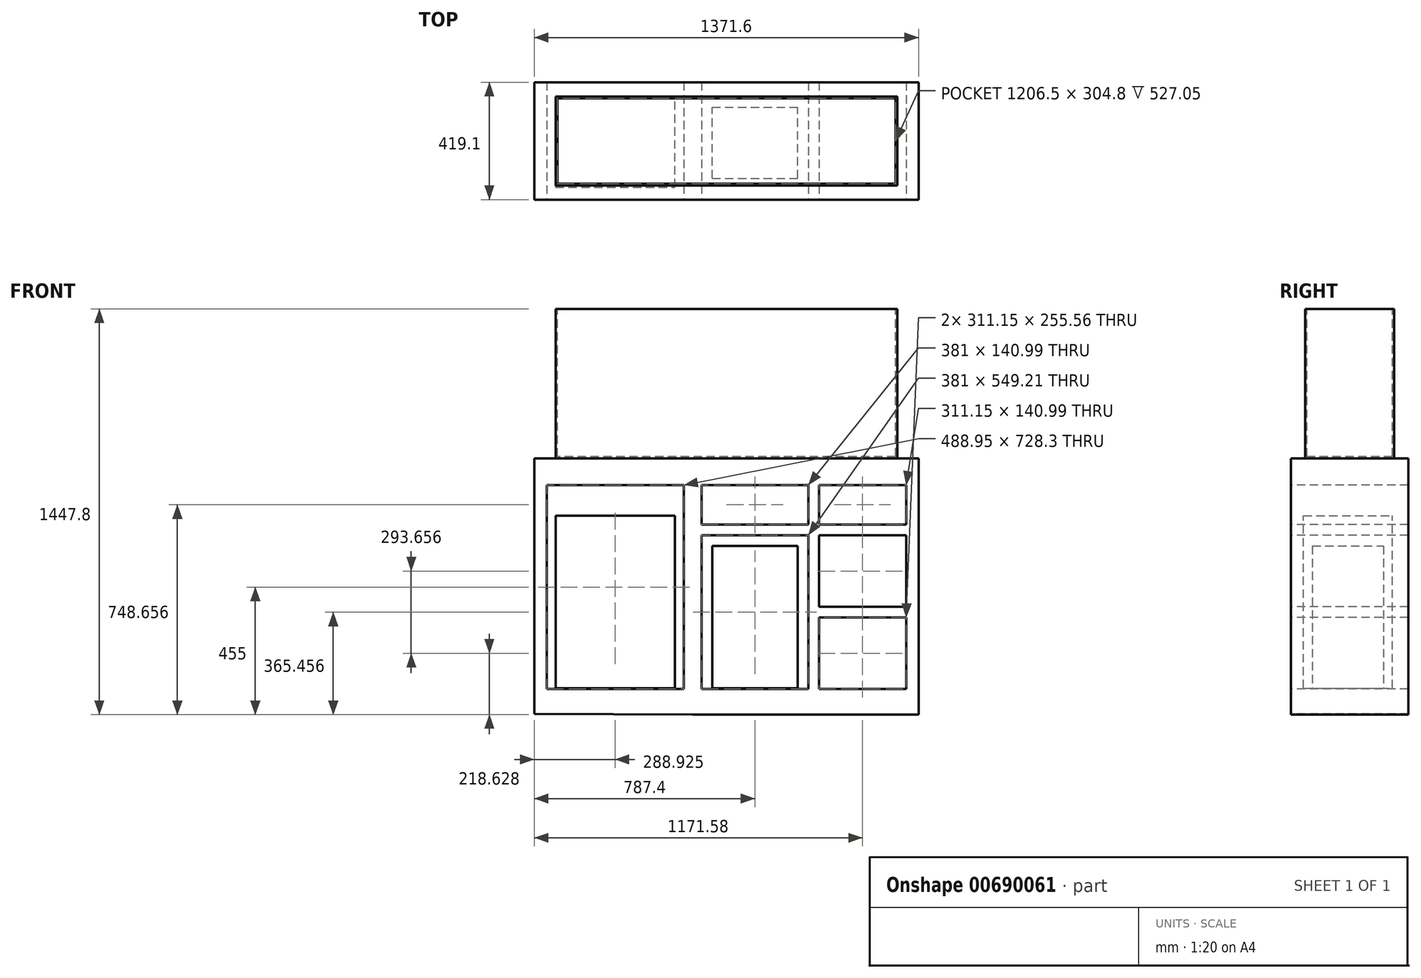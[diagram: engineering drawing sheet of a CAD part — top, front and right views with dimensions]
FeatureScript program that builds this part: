
annotation { "Feature Type Name" : "Feature", "Feature Type Description" : "" }
export const myFeature = defineFeature(function(context is Context, id is Id, definition is map)
    precondition{}
    {
        {
            var Q0;
            Q0=qCreatedBy(makeId("Front.planeOp"),FACE);
            var sketch = newSketch(context, id + "F0", { "sketchPlane" : qUnion([Q0])});
            skLineSegment(sketch, "E0", {"start": v(0, 0) * mm, "end": v(0, 533.4) * mm});
            skLineSegment(sketch, "E1", {"start": v(0, 533.4) * mm, "end": v(1219.2, 533.4) * mm});
            skLineSegment(sketch, "E2", {"start": v(1219.2, 533.4) * mm, "end": v(1219.2, 0) * mm});
            skLineSegment(sketch, "E3", {"start": v(1219.2, 0) * mm, "end": v(0, 0) * mm});
            skSolve(sketch);
        }
        {
            var Q0;
            Q0 = qSketchRegion(id + "F0", true);
            extrude(context, id + "F1", {"entities" : qUnion([Q0]), "depth" : 317.5 * mm, "offsetDistance" : 25.4 * mm});
        }
        {
            var Q0;
            Q0=makeQuery(id+"F1.opExtrude","SWEPT_FACE",FACE,{"disambiguationData":[OSD([sQuery(id+"F0.wireOp",EDGE,"E1")])]});
            var sketch = newSketch(context, id + "F2", { "sketchPlane" : qUnion([Q0])});
            skLineSegment(sketch, "E4", {"start": v(6.35, -6.35) * mm, "end": v(6.35, -311.15) * mm});
            skLineSegment(sketch, "E5", {"start": v(6.35, -311.15) * mm, "end": v(1212.85, -311.15) * mm});
            skLineSegment(sketch, "E6", {"start": v(1212.85, -311.15) * mm, "end": v(1212.85, -6.35) * mm});
            skLineSegment(sketch, "E7", {"start": v(1212.85, -6.35) * mm, "end": v(6.35, -6.35) * mm});
            skSolve(sketch);
        }
        {
            var Q0;
            Q0 = qSketchRegion(id + "F2", true);
            extrude(context, id + "F3", {"entities" : qUnion([Q0]), "operationType" : NewBodyOperationType.REMOVE, "oppositeDirection" : true, "depth" : 527.05 * mm, "offsetDistance" : 25.4 * mm});
        }
        {
            var Q0;
            Q0=makeQuery(id+"F1.opExtrude","CAP_FACE",FACE,{"disambiguationData":[OSD([sQuery(id+"F0.wireOp",EDGE,"E0"),sQuery(id+"F0.wireOp",EDGE,"E1"),sQuery(id+"F0.wireOp",EDGE,"E2"),sQuery(id+"F0.wireOp",EDGE,"E3")])],"isStart":false});
            var sketch = newSketch(context, id + "F4", { "sketchPlane" : qUnion([Q0])});
            skLineSegment(sketch, "E8", {"start": v(-76.2, 0) * mm, "end": v(1295.4, 0) * mm});
            skLineSegment(sketch, "E9", {"start": v(488.95, 0) * mm, "end": v(488.95, -914.4) * mm});
            skLineSegment(sketch, "E10", {"start": v(-76.2, 0) * mm, "end": v(-76.2, -912.45) * mm});
            skLineSegment(sketch, "E11", {"start": v(-76.2, -912.45) * mm, "end": v(488.95, -914.4) * mm});
            skLineSegment(sketch, "E12", {"start": v(1295.4, -914.4) * mm, "end": v(488.95, -914.4) * mm});
            skLineSegment(sketch, "E13", {"start": v(1295.4, 0) * mm, "end": v(1295.4, -914.4) * mm});
            skLineSegment(sketch, "E14", {"start": v(-76.2, -95.25) * mm, "end": v(1295.4, -95.25) * mm});
            skLineSegment(sketch, "E15", {"start": v(-76.2, -823.55) * mm, "end": v(1295.4, -823.55) * mm});
            skLineSegment(sketch, "E16", {"start": v(457.2, 0) * mm, "end": v(457.2, -914.4) * mm});
            skLineSegment(sketch, "E17", {"start": v(520.7, 0) * mm, "end": v(520.7, -912.45) * mm});
            skLineSegment(sketch, "E18", {"start": v(-31.75, 0) * mm, "end": v(-31.75, -912.45) * mm});
            skLineSegment(sketch, "E19", {"start": v(1250.95, 0) * mm, "end": v(1250.95, -914.4) * mm});
            skSolve(sketch);
        }
        {
            var Q0;
            {var subQ0=sQuery(id+"F4.wireOp",EDGE,"E14");var subQ1=sQuery(id+"F4.wireOp",EDGE,"E10");var subQ2=makeQuery(id+"F4.imprint","INTERSECT",VERTEX,{"derivedFrom":[subQ1,subQ0]});Q0=makeQuery(id+"F4.imprint","IMPRINT",FACE,{"disambiguationData":[TD([[makeQuery(id+"F4.imprint","IMPRINT",EDGE,{"disambiguationData":[TD([[subQ2,-1.0]])],"derivedFrom":subQ1}),1.0]])]});}
            var Q1;
            {var subQ1=sQuery(id+"F4.wireOp",EDGE,"E10");var subQ4=sQuery(id+"F4.wireOp",EDGE,"E11");var subQ5=makeQuery(id+"F4.imprint","INTERSECT",VERTEX,{"derivedFrom":[subQ1,subQ4]});Q1=makeQuery(id+"F4.imprint","IMPRINT",FACE,{"disambiguationData":[TD([[makeQuery(id+"F4.imprint","IMPRINT",EDGE,{"disambiguationData":[TD([[subQ5,1.0]])],"derivedFrom":subQ1}),1.0]])]});}
            var Q2;
            {var subQ0=sQuery(id+"F4.wireOp",EDGE,"E14");var subQ1=sQuery(id+"F4.wireOp",EDGE,"E9");var subQ2=makeQuery(id+"F4.imprint","INTERSECT",VERTEX,{"derivedFrom":[subQ1,subQ0]});Q2=makeQuery(id+"F4.imprint","IMPRINT",FACE,{"disambiguationData":[TD([[makeQuery(id+"F4.imprint","IMPRINT",EDGE,{"disambiguationData":[TD([[subQ2,-1.0]])],"derivedFrom":subQ1}),-1.0]])]});}
            var Q3;
            {var subQ0=sQuery(id+"F4.wireOp",EDGE,"E14");var subQ1=sQuery(id+"F4.wireOp",EDGE,"E9");var subQ2=makeQuery(id+"F4.imprint","INTERSECT",VERTEX,{"derivedFrom":[subQ1,subQ0]});Q3=makeQuery(id+"F4.imprint","IMPRINT",FACE,{"disambiguationData":[TD([[makeQuery(id+"F4.imprint","IMPRINT",EDGE,{"disambiguationData":[TD([[subQ2,-1.0]])],"derivedFrom":subQ1}),1.0]])]});}
            var Q4;
            {var subQ1=sQuery(id+"F4.wireOp",EDGE,"E9");var subQ3=sQuery(id+"F4.wireOp",EDGE,"E15");var subQ4=makeQuery(id+"F4.imprint","INTERSECT",VERTEX,{"derivedFrom":[subQ1,subQ3]});Q4=makeQuery(id+"F4.imprint","IMPRINT",FACE,{"disambiguationData":[TD([[makeQuery(id+"F4.imprint","IMPRINT",EDGE,{"disambiguationData":[TD([[subQ4,1.0]])],"derivedFrom":subQ3}),-1.0]])]});}
            var Q5;
            {var subQ0=sQuery(id+"F4.wireOp",EDGE,"E15");var subQ1=makeQuery(id+"F4.imprint","INTERSECT",VERTEX,{"derivedFrom":[subQ0,sQuery(id+"F4.wireOp",EDGE,"E17")]});Q5=makeQuery(id+"F4.imprint","IMPRINT",FACE,{"disambiguationData":[TD([[makeQuery(id+"F4.imprint","IMPRINT",EDGE,{"disambiguationData":[TD([[subQ1,1.0]])],"derivedFrom":subQ0}),-1.0]])]});}
            var Q6;
            {var subQ0=sQuery(id+"F4.wireOp",EDGE,"E13");var subQ1=sQuery(id+"F4.wireOp",EDGE,"E12");var subQ2=makeQuery(id+"F4.imprint","INTERSECT",VERTEX,{"derivedFrom":[subQ1,subQ0]});Q6=makeQuery(id+"F4.imprint","IMPRINT",FACE,{"disambiguationData":[TD([[makeQuery(id+"F4.imprint","IMPRINT",EDGE,{"disambiguationData":[TD([[subQ2,-1.0]])],"derivedFrom":subQ1}),-1.0]])]});}
            var Q7;
            {var subQ0=sQuery(id+"F4.wireOp",EDGE,"E14");var subQ1=sQuery(id+"F4.wireOp",EDGE,"E13");var subQ2=makeQuery(id+"F4.imprint","INTERSECT",VERTEX,{"derivedFrom":[subQ1,subQ0]});Q7=makeQuery(id+"F4.imprint","IMPRINT",FACE,{"disambiguationData":[TD([[makeQuery(id+"F4.imprint","IMPRINT",EDGE,{"disambiguationData":[TD([[subQ2,-1.0]])],"derivedFrom":subQ1}),-1.0]])]});}
            var Q8;
            {var subQ0=sQuery(id+"F4.wireOp",EDGE,"E13");var subQ1=sQuery(id+"F4.wireOp",EDGE,"E8");var subQ2=makeQuery(id+"F4.imprint","INTERSECT",VERTEX,{"derivedFrom":[subQ1,subQ0]});Q8=makeQuery(id+"F4.imprint","IMPRINT",FACE,{"disambiguationData":[TD([[makeQuery(id+"F4.imprint","IMPRINT",EDGE,{"disambiguationData":[TD([[subQ2,1.0]])],"derivedFrom":subQ1}),-1.0]])]});}
            var Q9;
            {var subQ0=sQuery(id+"F4.wireOp",EDGE,"E17");var subQ1=sQuery(id+"F4.wireOp",EDGE,"E8");var subQ2=makeQuery(id+"F4.imprint","INTERSECT",VERTEX,{"derivedFrom":[subQ1,subQ0]});Q9=makeQuery(id+"F4.imprint","IMPRINT",FACE,{"disambiguationData":[TD([[makeQuery(id+"F4.imprint","IMPRINT",EDGE,{"disambiguationData":[TD([[subQ2,1.0]])],"derivedFrom":subQ1}),1.0]])]});}
            var Q10;
            {var subQ1=sQuery(id+"F4.wireOp",EDGE,"E8");var subQ5=sQuery(id+"F4.wireOp",EDGE,"E18");var subQ8=makeQuery(id+"F4.imprint","INTERSECT",VERTEX,{"derivedFrom":[subQ1,subQ5]});Q10=makeQuery(id+"F4.imprint","IMPRINT",FACE,{"disambiguationData":[TD([[makeQuery(id+"F4.imprint","IMPRINT",EDGE,{"disambiguationData":[TD([[subQ8,-1.0]])],"derivedFrom":subQ1}),-1.0]])]});}
            var Q11;
            {var subQ0=sQuery(id+"F4.wireOp",EDGE,"E10");var subQ1=sQuery(id+"F4.wireOp",EDGE,"E8");var subQ2=makeQuery(id+"F4.imprint","INTERSECT",VERTEX,{"derivedFrom":[subQ1,subQ0]});Q11=makeQuery(id+"F4.imprint","IMPRINT",FACE,{"disambiguationData":[TD([[makeQuery(id+"F4.imprint","IMPRINT",EDGE,{"disambiguationData":[TD([[subQ2,-1.0]])],"derivedFrom":subQ1}),-1.0]])]});}
            var Q12;
            {var subQ0=sQuery(id+"F4.wireOp",EDGE,"E9");var subQ1=sQuery(id+"F4.wireOp",EDGE,"E8");var subQ2=makeQuery(id+"F4.imprint","INTERSECT",VERTEX,{"derivedFrom":[subQ1,subQ0]});Q12=makeQuery(id+"F4.imprint","IMPRINT",FACE,{"disambiguationData":[TD([[makeQuery(id+"F4.imprint","IMPRINT",EDGE,{"disambiguationData":[TD([[subQ2,1.0]])],"derivedFrom":subQ1}),1.0]])]});}
            var Q13;
            {var subQ0=sQuery(id+"F4.wireOp",EDGE,"E9");var subQ1=sQuery(id+"F4.wireOp",EDGE,"E8");var subQ2=makeQuery(id+"F4.imprint","INTERSECT",VERTEX,{"derivedFrom":[subQ1,subQ0]});Q13=makeQuery(id+"F4.imprint","IMPRINT",FACE,{"disambiguationData":[TD([[makeQuery(id+"F4.imprint","IMPRINT",EDGE,{"disambiguationData":[TD([[subQ2,-1.0]])],"derivedFrom":subQ1}),1.0]])]});}
            extrude(context, id + "F5", {"entities" : qUnion([Q0, Q1, Q2, Q3, Q4, Q5, Q6, Q7, Q8, Q9, Q10, Q11, Q12, Q13]), "operationType" : NewBodyOperationType.ADD, "oppositeDirection" : true, "depth" : 368.3 * mm, "offsetDistance" : 25.4 * mm, "hasSecondDirection" : true, "secondDirectionOppositeDirection" : false, "secondDirectionDepth" : 50.8 * mm});
        }
        {
            var Q0;
            Q0=makeQuery(id+"F5.opExtrude","CAP_FACE",FACE,{"disambiguationData":[OSD([sQuery(id+"F4.wireOp",EDGE,"E8"),sQuery(id+"F4.wireOp",EDGE,"E10"),sQuery(id+"F4.wireOp",EDGE,"E11"),sQuery(id+"F4.wireOp",EDGE,"E12"),sQuery(id+"F4.wireOp",EDGE,"E13"),sQuery(id+"F4.wireOp",EDGE,"E14"),sQuery(id+"F4.wireOp",EDGE,"E15"),sQuery(id+"F4.wireOp",EDGE,"E18"),sQuery(id+"F4.wireOp",EDGE,"E19")])],"isStart":true});
            var sketch = newSketch(context, id + "F6", { "sketchPlane" : qUnion([Q0])});
            skSolve(sketch);
        }
        {
            var Q0;
            {var subQ0=sQuery(id+"F4.wireOp",EDGE,"E15");Q0=makeQuery(id+"FelftkuU2XWx3Qa_1.boolean.opBoolean","MERGE",FACE,{"derivedFrom":[makeQuery(id+"F5.opExtrude","CAP_FACE",FACE,{"disambiguationData":[OSD([sQuery(id+"F4.wireOp",EDGE,"E8"),sQuery(id+"F4.wireOp",EDGE,"E10"),sQuery(id+"F4.wireOp",EDGE,"E11"),sQuery(id+"F4.wireOp",EDGE,"E12"),sQuery(id+"F4.wireOp",EDGE,"E13"),sQuery(id+"F4.wireOp",EDGE,"E14"),subQ0,sQuery(id+"F4.wireOp",EDGE,"E18"),sQuery(id+"F4.wireOp",EDGE,"E19")])],"isStart":true}),makeQuery(id+"FelftkuU2XWx3Qa_1.opExtrude","CAP_FACE",FACE,{"disambiguationData":[OSD([subQ0,sQuery(id+"F6.wireOp",EDGE,"Hjd6XBfF-dVlF-Pm7Q-uADI-go517BE28nij"),sQuery(id+"F6.wireOp",EDGE,"cSgCX02E-Zrxk-a7Yq-Ogc6-joIkRk6Krvnl"),sQuery(id+"F6.wireOp",EDGE,"0acloNvj-Bg05-ruuI-fCY6-iIz3YAx0FRrr"),sQuery(id+"F6.wireOp",EDGE,"pUvd6JdS-TNx4-0T37-JsWi-MApJu50DnG9t")])],"isStart":true})]});}
            cPlane(context, id + "F7", {"entities" : qUnion([Q0]), "cplaneType" : CPlaneType.OFFSET, "offset" : 203.2 * mm, "oppositeDirection" : true, "width" : 152.4 * mm, "height" : 152.4 * mm});
        }
        {
            var Q0;
            Q0=qCreatedBy(id+"F7.planeOp",FACE);
            var sketch = newSketch(context, id + "F8", { "sketchPlane" : qUnion([Q0])});
            skLineSegment(sketch, "E20.bottom", {"start": v(0, -820.44) * mm, "end": v(425.45, -820.44) * mm});
            skLineSegment(sketch, "E20.top", {"start": v(0, -204.49) * mm, "end": v(425.45, -204.49) * mm});
            skLineSegment(sketch, "E20.left", {"start": v(0, -820.44) * mm, "end": v(0, -204.49) * mm});
            skLineSegment(sketch, "E20.right", {"start": v(425.45, -820.44) * mm, "end": v(425.45, -204.49) * mm});
            skSolve(sketch);
        }
        {
            var Q0;
            Q0 = qSketchRegion(id + "F8", true);
            extrude(context, id + "F9", {"entities" : qUnion([Q0]), "depth" : 158.75 * mm, "offsetDistance" : 25.4 * mm, "hasSecondDirection" : true, "secondDirectionOppositeDirection" : true, "secondDirectionDepth" : 158.75 * mm});
        }
        {
            var Q0;
            Q0=qCreatedBy(id+"F7.planeOp",FACE);
            var sketch = newSketch(context, id + "F10", { "sketchPlane" : qUnion([Q0])});
            skLineSegment(sketch, "E21.bottom", {"start": v(558.8, -312.44) * mm, "end": v(863.6, -312.44) * mm});
            skLineSegment(sketch, "E21.top", {"start": v(558.8, -820.44) * mm, "end": v(863.6, -820.44) * mm});
            skLineSegment(sketch, "E21.left", {"start": v(558.8, -312.44) * mm, "end": v(558.8, -820.44) * mm});
            skLineSegment(sketch, "E21.right", {"start": v(863.6, -312.44) * mm, "end": v(863.6, -820.44) * mm});
            skSolve(sketch);
        }
        {
            var Q0;
            Q0 = qSketchRegion(id + "F10", true);
            extrude(context, id + "F11", {"entities" : qUnion([Q0]), "depth" : 127 * mm, "offsetDistance" : 25.4 * mm, "hasSecondDirection" : true, "secondDirectionOppositeDirection" : true, "secondDirectionDepth" : 127 * mm});
        }
        {
            var Q0;
            Q0=makeQuery(id+"F6.imprint","IMPRINT",FACE,{"disambiguationData":[TD([[makeQuery(id+"F6.imprint","IMPRINT",EDGE,{"derivedFrom":makeQuery(id+"F5.opExtrude","CAP_EDGE",EDGE,{"disambiguationData":[OSD([sQuery(id+"F4.wireOp",EDGE,"E8")])],"isStart":true})}),-1.0]])]});
            var sketch = newSketch(context, id + "F12", { "sketchPlane" : qUnion([Q0])});
            skLineSegment(sketch, "E22.bottom", {"start": v(520.7, -236.24) * mm, "end": v(1250.95, -236.24) * mm});
            skLineSegment(sketch, "E22.top", {"start": v(520.7, -274.34) * mm, "end": v(1250.95, -274.34) * mm});
            skLineSegment(sketch, "E22.left", {"start": v(520.7, -236.24) * mm, "end": v(520.7, -274.34) * mm});
            skLineSegment(sketch, "E22.right", {"start": v(1250.95, -236.24) * mm, "end": v(1250.95, -274.34) * mm});
            skLineSegment(sketch, "E23.bottom", {"start": v(901.7, -95.25) * mm, "end": v(939.8, -95.25) * mm});
            skLineSegment(sketch, "E23.top", {"start": v(901.7, -823.55) * mm, "end": v(939.8, -823.55) * mm});
            skLineSegment(sketch, "E23.left", {"start": v(901.7, -95.25) * mm, "end": v(901.7, -823.55) * mm});
            skLineSegment(sketch, "E23.right", {"start": v(939.8, -95.25) * mm, "end": v(939.8, -823.55) * mm});
            skLineSegment(sketch, "E24.bottom", {"start": v(939.8, -529.9) * mm, "end": v(1250.95, -529.9) * mm});
            skLineSegment(sketch, "E24.top", {"start": v(939.8, -568) * mm, "end": v(1250.95, -568) * mm});
            skLineSegment(sketch, "E24.left", {"start": v(939.8, -529.9) * mm, "end": v(939.8, -568) * mm});
            skLineSegment(sketch, "E24.right", {"start": v(1250.95, -529.9) * mm, "end": v(1250.95, -568) * mm});
            skSolve(sketch);
        }
        {
            var Q0;
            Q0 = qSketchRegion(id + "F12", true);
            var Q1;
            Q1=makeQuery(id+"F5.opExtrude","CAP_FACE",FACE,{"disambiguationData":[OSD([sQuery(id+"F4.wireOp",EDGE,"E8"),sQuery(id+"F4.wireOp",EDGE,"E10"),sQuery(id+"F4.wireOp",EDGE,"E11"),sQuery(id+"F4.wireOp",EDGE,"E12"),sQuery(id+"F4.wireOp",EDGE,"E13"),sQuery(id+"F4.wireOp",EDGE,"E14"),sQuery(id+"F4.wireOp",EDGE,"E15"),sQuery(id+"F4.wireOp",EDGE,"E16"),sQuery(id+"F4.wireOp",EDGE,"E17"),sQuery(id+"F4.wireOp",EDGE,"E18"),sQuery(id+"F4.wireOp",EDGE,"E19")])],"isStart":false});
            extrude(context, id + "F13", {"entities" : qUnion([Q0]), "operationType" : NewBodyOperationType.ADD, "endBound" : BoundingType.UP_TO_SURFACE, "oppositeDirection" : true, "depth" : 25.4 * mm, "endBoundEntityFace" : qUnion([Q1]), "offsetDistance" : 25.4 * mm});
        }
    });
